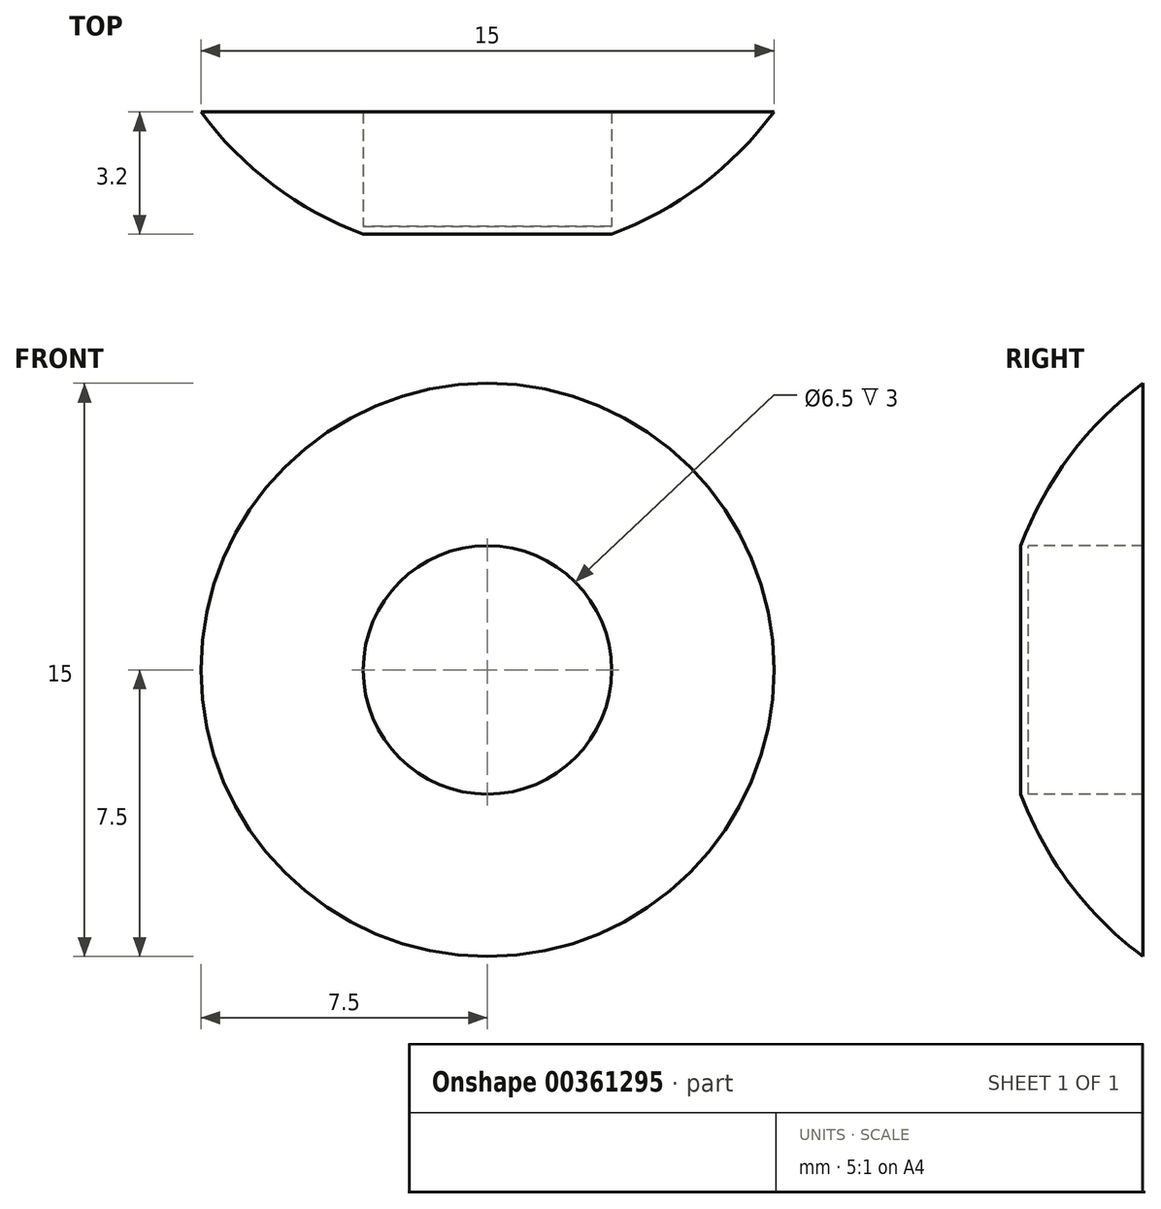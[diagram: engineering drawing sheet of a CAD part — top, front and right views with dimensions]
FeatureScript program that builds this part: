
annotation { "Feature Type Name" : "Feature", "Feature Type Description" : "" }
export const myFeature = defineFeature(function(context is Context, id is Id, definition is map)
    precondition{}
    {
        {
            var Q0;
            Q0=qCreatedBy(makeId("Top.planeOp"),FACE);
            var sketch = newSketch(context, id + "F0", { "sketchPlane" : qUnion([Q0])});
            skCircle(sketch, "E0", {"center": v(0, 0) * mm, "radius": 3.25 * mm, "construction": true});
            skCircle(sketch, "E1", {"center": v(0, 0) * mm, "radius": 7.5 * mm, "construction": true});
            skPoint(sketch, "E2.first.point", {"position": v(-7.35, 1.5) * mm});
            skPoint(sketch, "E2.second.point", {"position": v(7.35, 1.5) * mm});
            skPoint(sketch, "E2.third.point", {"position": v(-3.25, 0) * mm});
            skLineSegment(sketch, "E3", {"start": v(-3.25, 0) * mm, "end": v(0, 0) * mm});
            skLineSegment(sketch, "E4", {"start": v(0, 0) * mm, "end": v(0, 0.2) * mm});
            skLineSegment(sketch, "E5", {"start": v(0, 0.2) * mm, "end": v(-3.25, 0.2) * mm});
            skLineSegment(sketch, "E6", {"start": v(-3.25, 0.2) * mm, "end": v(-3.25, 3.2) * mm});
            skLineSegment(sketch, "E7", {"start": v(-7.5, 0) * mm, "end": v(-7.5, 5.2) * mm, "construction": true});
            skLineSegment(sketch, "E8", {"start": v(7.5, 0) * mm, "end": v(7.5, 5.2) * mm, "construction": true});
            skLineSegment(sketch, "E9", {"start": v(-3.25, 3.2) * mm, "end": v(12.75, 3.2) * mm, "construction": true});
            skLineSegment(sketch, "E10", {"start": v(-3.25, 3.2) * mm, "end": v(-7.5, 3.2) * mm});
            skArc(sketch, "E11", {"start": v(-7.5, 3.2) * mm, "mid": v(-5.6, 1.3) * mm, "end": v(-3.25, 0) * mm});
            skPoint(sketch, "E11.first.point", {"position": v(-7.5, 3.2) * mm});
            skPoint(sketch, "E11.third.point", {"position": v(7.5, 3.2) * mm});
            skSolve(sketch);
        }
        {
            var Q0;
            Q0=makeQuery(id+"F0.imprint","IMPRINT",FACE,{"disambiguationData":[TD([[makeQuery(id+"F0.imprint","IMPRINT",EDGE,{"derivedFrom":sQuery(id+"F0.wireOp",EDGE,"E3")}),1.0]])]});
            var Q1;
            Q1=sQuery(id+"F0.wireOp",EDGE,"E4");
            revolve(context, id + "F1", {"entities" : qUnion([Q0]), "axis" : qUnion([Q1]), "revolveType" : RevolveType.FULL});
        }
    });
